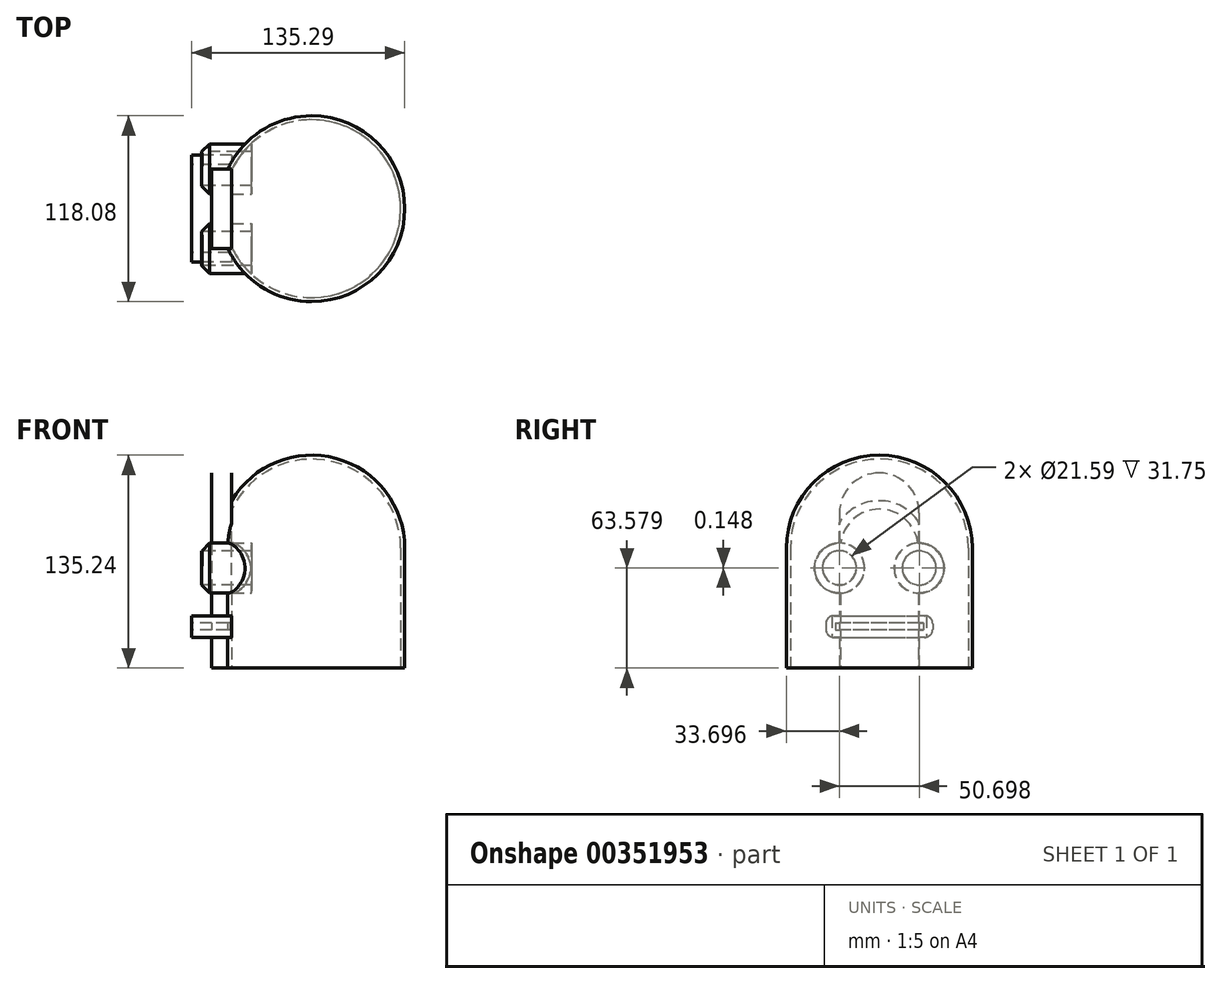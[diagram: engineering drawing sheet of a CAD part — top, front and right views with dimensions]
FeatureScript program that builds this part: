
annotation { "Feature Type Name" : "Feature", "Feature Type Description" : "" }
export const myFeature = defineFeature(function(context is Context, id is Id, definition is map)
    precondition{}
    {
        {
            var Q0;
            Q0=qCreatedBy(makeId("Top.planeOp"),FACE);
            var sketch = newSketch(context, id + "F0", { "sketchPlane" : qUnion([Q0])});
            skCircle(sketch, "E0", {"center": v(0, 0) * mm, "radius": 59.04 * mm});
            skSolve(sketch);
        }
        {
            var Q0;
            Q0 = qSketchRegion(id + "F0", true);
            extrude(context, id + "F1", {"entities" : qUnion([Q0]), "depth" : 76.2 * mm});
        }
        {
            var Q0;
            Q0=makeQuery(id+"F1.opExtrude","CAP_FACE",FACE,{"disambiguationData":[OSD([sQuery(id+"F0.wireOp",EDGE,"E0")])],"isStart":false});
            var sketch = newSketch(context, id + "F2", { "sketchPlane" : qUnion([Q0])});
            skArc(sketch, "E1", {"start": v(0, -59.04) * mm, "mid": v(-59.04, 0) * mm, "end": v(0, 59.04) * mm});
            skLineSegment(sketch, "E2", {"start": v(0, 59.04) * mm, "end": v(0, -59.04) * mm});
            skSolve(sketch);
        }
        {
            var Q0;
            Q0 = qSketchRegion(id + "F2", true);
            var Q1;
            Q1=sQuery(id+"F2.wireOp",EDGE,"E2");
            revolve(context, id + "F3", {"operationType" : NewBodyOperationType.ADD, "entities" : qUnion([Q0]), "axis" : qUnion([Q1]), "revolveType" : RevolveType.ONE_DIRECTION, "oppositeDirection" : true, "angle" : 180 * degree});
        }
        {
            var Q0;
            Q0=qCreatedBy(makeId("Top.planeOp"),FACE);
            var sketch = newSketch(context, id + "F4", { "sketchPlane" : qUnion([Q0])});
            skLineSegment(sketch, "E3.bottom", {"start": v(-63.55, -25.29) * mm, "end": v(-50.8, -25.29) * mm});
            skLineSegment(sketch, "E3.top", {"start": v(-63.55, 25.29) * mm, "end": v(-50.8, 25.29) * mm});
            skLineSegment(sketch, "E3.left", {"start": v(-63.55, -25.29) * mm, "end": v(-63.55, 25.29) * mm});
            skLineSegment(sketch, "E3.right", {"start": v(-50.8, -25.29) * mm, "end": v(-50.8, 25.29) * mm});
            skPoint(sketch, "E3.middle", {"position": v(-57.17, 0) * mm});
            skSolve(sketch);
        }
        {
            var Q0;
            Q0=makeQuery(id+"F6.boolean.opBoolean","MERGE",FACE,{"derivedFrom":[makeQuery(id+"F1.opExtrude","CAP_FACE",FACE,{"disambiguationData":[OSD([sQuery(id+"F0.wireOp",EDGE,"E0")])],"isStart":true}),makeQuery(id+"F6.opExtrude","CAP_FACE",FACE,{"disambiguationData":[OSD([sQuery(id+"F4.wireOp",EDGE,"E3.bottom"),sQuery(id+"F4.wireOp",EDGE,"E3.top"),sQuery(id+"F4.wireOp",EDGE,"E3.left"),sQuery(id+"F4.wireOp",EDGE,"E3.right")])],"isStart":true})]});
            shell(context, id + "F5", {"entities" : qUnion([Q0]), "thickness" : 2.54 * mm});
        }
        {
            var Q0;
            Q0 = qSketchRegion(id + "F4", true);
            extrude(context, id + "F6", {"entities" : qUnion([Q0]), "operationType" : NewBodyOperationType.ADD, "depth" : 123.95 * mm});
        }
        {
            var Q0;
            Q0=makeQuery(id+"F6.opExtrude","CAP_EDGE",EDGE,{"disambiguationData":[OSD([sQuery(id+"F4.wireOp",EDGE,"E3.top")])],"isStart":false});
            var Q1;
            Q1=makeQuery(id+"F6.opExtrude","CAP_EDGE",EDGE,{"disambiguationData":[OSD([sQuery(id+"F4.wireOp",EDGE,"E3.bottom")])],"isStart":false});
            fillet(context, id + "F7", {"entities" : qUnion([Q0, Q1]), "radius" : 25.4 * mm, "tangentPropagation" : true, "allowEdgeOverflow" : false});
        }
        {
            var Q0;
            Q0=makeQuery(id+"F6.opExtrude","SWEPT_FACE",FACE,{"disambiguationData":[OSD([sQuery(id+"F4.wireOp",EDGE,"E3.left")])]});
            var sketch = newSketch(context, id + "F8", { "sketchPlane" : qUnion([Q0])});
            skLineSegment(sketch, "E4", {"start": v(0, 123.95) * mm, "end": v(0, 0) * mm, "construction": true});
            skLineSegment(sketch, "E5", {"start": v(-25.29, 63.5) * mm, "end": v(25.29, 63.5) * mm});
            skCircle(sketch, "E6", {"center": v(25.29, 63.5) * mm, "radius": 15.88 * mm});
            skSolve(sketch);
        }
        {
            var Q0;
            {var subQ0=sQuery(id+"F8.wireOp",EDGE,"E6");var subQ1=makeQuery(id+"F6.opExtrude","SWEPT_EDGE",EDGE,{"disambiguationData":[OSD([sQuery(id+"F4.wireOp",EDGE,"E3.bottom"),sQuery(id+"F4.wireOp",EDGE,"E3.left")])]});var subQ2=makeQuery(id+"F8.imprint","INTERSECT",VERTEX,{"disambiguationData":[OD(0.0)],"derivedFrom":[subQ1,subQ0]});Q0=makeQuery(id+"F8.imprint","IMPRINT",FACE,{"disambiguationData":[TD([[makeQuery(id+"F8.imprint","IMPRINT",EDGE,{"disambiguationData":[TD([[subQ2,1.0]])],"derivedFrom":subQ0}),1.0]])]});}
            var Q1;
            {var subQ0=sQuery(id+"F8.wireOp",EDGE,"E5");var subQ3=sQuery(id+"F8.wireOp",EDGE,"E6");var subQ4=makeQuery(id+"F8.imprint","INTERSECT",VERTEX,{"derivedFrom":[subQ0,subQ3]});Q1=makeQuery(id+"F8.imprint","IMPRINT",FACE,{"disambiguationData":[TD([[makeQuery(id+"F8.imprint","IMPRINT",EDGE,{"disambiguationData":[TD([[subQ4,-1.0]])],"derivedFrom":subQ0}),1.0]])]});}
            var Q2;
            {var subQ0=sQuery(id+"F8.wireOp",EDGE,"E5");var subQ3=sQuery(id+"F8.wireOp",EDGE,"E6");var subQ4=makeQuery(id+"F8.imprint","INTERSECT",VERTEX,{"derivedFrom":[subQ0,subQ3]});Q2=makeQuery(id+"F8.imprint","IMPRINT",FACE,{"disambiguationData":[TD([[makeQuery(id+"F8.imprint","IMPRINT",EDGE,{"disambiguationData":[TD([[subQ4,-1.0]])],"derivedFrom":subQ0}),-1.0]])]});}
            var Q3;
            Q3=sQuery(id+"F8.wireOp",EDGE,"E6");
            extrude(context, id + "F9", {"entities" : qUnion([Q0, Q1, Q2]), "surfaceEntities" : qUnion([Q3]), "depth" : 6.35 * mm, "hasSecondDirection" : true, "secondDirectionOppositeDirection" : true, "secondDirectionDepth" : 25.4 * mm});
        }
        {
            var Q0;
            Q0=makeQuery(id+"F9.opExtrude","CAP_FACE",FACE,{"disambiguationData":[OSD([sQuery(id+"F8.wireOp",EDGE,"E6")])],"isStart":false});
            var sketch = newSketch(context, id + "F10", { "sketchPlane" : qUnion([Q0])});
            skLineSegment(sketch, "E7", {"start": v(25.34, 79.37) * mm, "end": v(25.34, 47.63) * mm, "construction": true});
            skLineSegment(sketch, "E8", {"start": v(9.41, 63.73) * mm, "end": v(41.16, 63.73) * mm, "construction": true});
            skCircle(sketch, "E9", {"center": v(25.34, 63.73) * mm, "radius": 11.24 * mm});
            skSolve(sketch);
        }
        {
            var Q0;
            Q0=makeQuery(id+"F9.opExtrude","CAP_EDGE",EDGE,{"disambiguationData":[OSD([sQuery(id+"F8.wireOp",EDGE,"E6")])],"isStart":false});
            chamfer(context, id + "F11", {"entities" : qUnion([Q0]), "width" : 5.08 * mm, "tangentPropagation" : true});
        }
        {
            var Q0;
            Q0=makeQuery(id+"F9.opExtrude","SWEPT_BODY",BODY,{"disambiguationData":[OSD([sQuery(id+"F8.wireOp",EDGE,"E6")])]});
            var Q1;
            Q1=qCreatedBy(makeId("Front.planeOp"),FACE);
            mirror(context, id + "F12", {"operationType" : NewBodyOperationType.ADD, "entities" : qUnion([Q0]), "mirrorPlane" : qUnion([Q1])});
        }
        {
            var Q0;
            Q0=sQuery(id+"F10.wireOp",VERTEX,"E9.center");
            var Q1;
            Q1=makeQuery(id+"F1.opExtrude","SWEPT_BODY",BODY,{"disambiguationData":[OSD([sQuery(id+"F0.wireOp",EDGE,"E0")])]});
            hole(context, id + "F13", {"style" : HoleStyle.SIMPLE, "endStyle" : HoleEndStyle.BLIND, "holeDiameter" : 21.59 * mm, "holeDepth" : 101.6 * mm, "isTappedThrough" : true, "tappedDepth" : 12.7 * mm, "tapClearance" : 3, "startFromSketch" : true, "locations" : qUnion([Q0]), "scope" : qUnion([Q1])});
        }
        {
            var Q0;
            Q0=makeQuery(id+"F12.opPattern","COPY",FACE,{"derivedFrom":makeQuery(id+"F9.opExtrude","CAP_FACE",FACE,{"disambiguationData":[OSD([sQuery(id+"F8.wireOp",EDGE,"E6")])],"isStart":false}),"instanceName":"1"});
            var sketch = newSketch(context, id + "F14", { "sketchPlane" : qUnion([Q0])});
            skLineSegment(sketch, "E10", {"start": v(-14.5, 63.58) * mm, "end": v(-36.08, 63.58) * mm, "construction": true});
            skLineSegment(sketch, "E11", {"start": v(-25.35, 74.3) * mm, "end": v(-25.35, 52.7) * mm, "construction": true});
            skCircle(sketch, "E12", {"center": v(-25.35, 63.58) * mm, "radius": 6.56 * mm});
            skSolve(sketch);
        }
        {
            var Q0;
            Q0=sQuery(id+"F14.wireOp",VERTEX,"E12.center");
            var Q1;
            Q1=makeQuery(id+"F1.opExtrude","SWEPT_BODY",BODY,{"disambiguationData":[OSD([sQuery(id+"F0.wireOp",EDGE,"E0")])]});
            hole(context, id + "F15", {"style" : HoleStyle.SIMPLE, "endStyle" : HoleEndStyle.BLIND, "holeDiameter" : 21.59 * mm, "holeDepth" : 101.6 * mm, "isTappedThrough" : true, "tappedDepth" : 12.7 * mm, "tapClearance" : 3, "startFromSketch" : true, "locations" : qUnion([Q0]), "scope" : qUnion([Q1])});
        }
        {
            var Q0;
            Q0=makeQuery(id+"F6.opExtrude","SWEPT_FACE",FACE,{"disambiguationData":[OSD([sQuery(id+"F4.wireOp",EDGE,"E3.left")])]});
            var sketch = newSketch(context, id + "F16", { "sketchPlane" : qUnion([Q0])});
            skLineSegment(sketch, "E13.bottom", {"start": v(33.93, 33.24) * mm, "end": v(-33.93, 33.24) * mm});
            skLineSegment(sketch, "E13.top", {"start": v(33.93, 19.54) * mm, "end": v(-33.93, 19.54) * mm});
            skLineSegment(sketch, "E13.left", {"start": v(33.93, 33.24) * mm, "end": v(33.93, 19.54) * mm});
            skLineSegment(sketch, "E13.right", {"start": v(-33.93, 33.24) * mm, "end": v(-33.93, 19.54) * mm});
            skPoint(sketch, "E13.middle", {"position": v(0, 26.39) * mm});
            skLineSegment(sketch, "E14.bottom", {"start": v(-27.95, 28.65) * mm, "end": v(27.95, 28.65) * mm});
            skLineSegment(sketch, "E14.top", {"start": v(-27.95, 24.12) * mm, "end": v(27.95, 24.12) * mm});
            skLineSegment(sketch, "E14.left", {"start": v(-27.95, 28.65) * mm, "end": v(-27.95, 24.12) * mm});
            skLineSegment(sketch, "E14.right", {"start": v(27.95, 28.65) * mm, "end": v(27.95, 24.12) * mm});
            skSolve(sketch);
        }
        {
            var Q0;
            Q0 = qSketchRegion(id + "F16", true);
            var Q1;
            {var subQ0=sQuery(id+"F0.wireOp",EDGE,"E0");var subQ1=sQuery(id+"F4.wireOp",EDGE,"E3.right");Q1=makeQuery(id+"F6.boolean.opBoolean","SPLIT",FACE,{"disambiguationData":[TD([makeQuery(id+"F1.opExtrude","CAP_FACE",FACE,{"disambiguationData":[OSD([subQ0])],"isStart":true})])],"derivedFrom":makeQuery(id+"F6.opExtrude","SWEPT_FACE",FACE,{"disambiguationData":[OSD([subQ1])]})});}
            extrude(context, id + "F17", {"entities" : qUnion([Q0]), "operationType" : NewBodyOperationType.ADD, "endBound" : BoundingType.SYMMETRIC, "oppositeDirection" : true, "endBoundEntityFace" : qUnion([Q1]), "depth" : 25.4 * mm});
        }
        {
            var Q0;
            Q0=makeQuery(id+"F17.opExtrude","SWEPT_EDGE",EDGE,{"disambiguationData":[OSD([sQuery(id+"F16.wireOp",EDGE,"E13.bottom"),sQuery(id+"F16.wireOp",EDGE,"E13.left")])]});
            var Q1;
            Q1=makeQuery(id+"F17.opExtrude","SWEPT_EDGE",EDGE,{"disambiguationData":[OSD([sQuery(id+"F16.wireOp",EDGE,"E13.top"),sQuery(id+"F16.wireOp",EDGE,"E13.left")])]});
            var Q2;
            Q2=makeQuery(id+"F17.opExtrude","SWEPT_EDGE",EDGE,{"disambiguationData":[OSD([sQuery(id+"F16.wireOp",EDGE,"E13.bottom"),sQuery(id+"F16.wireOp",EDGE,"E13.right")])]});
            var Q3;
            Q3=makeQuery(id+"F17.opExtrude","SWEPT_EDGE",EDGE,{"disambiguationData":[OSD([sQuery(id+"F16.wireOp",EDGE,"E13.top"),sQuery(id+"F16.wireOp",EDGE,"E13.right")])]});
            fillet(context, id + "F18", {"entities" : qUnion([Q0, Q1, Q2, Q3]), "radius" : 5.08 * mm, "tangentPropagation" : true, "allowEdgeOverflow" : false});
        }
    });
